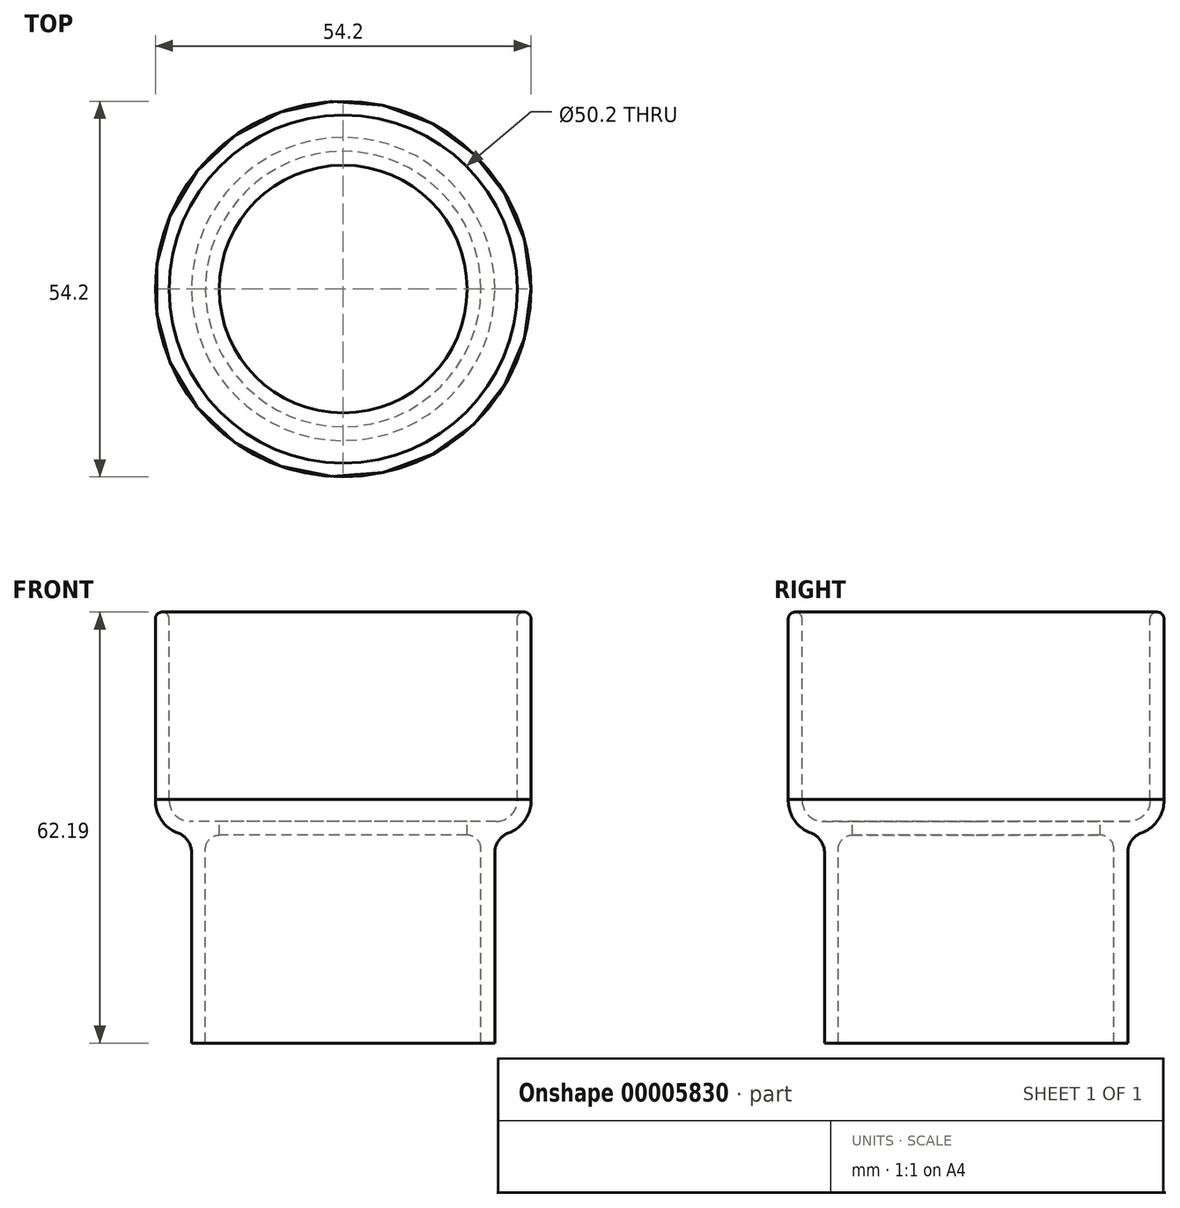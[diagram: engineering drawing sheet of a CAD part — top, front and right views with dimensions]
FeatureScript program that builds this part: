
annotation { "Feature Type Name" : "Feature", "Feature Type Description" : "" }
export const myFeature = defineFeature(function(context is Context, id is Id, definition is map)
    precondition{}
    {
        {
            var Q0;
            Q0=qCreatedBy(makeId("Front.planeOp"),FACE);
            var sketch = newSketch(context, id + "F0", { "sketchPlane" : qUnion([Q0])});
            skLineSegment(sketch, "E0.right", {"start": v(-27.1, 62.19) * mm, "end": v(-27.1, 35.18) * mm});
            skLineSegment(sketch, "E1", {"start": v(-25.1, 62.19) * mm, "end": v(-25.1, 35) * mm});
            skLineSegment(sketch, "E2", {"start": v(-19.88, 0) * mm, "end": v(-19.88, 28) * mm});
            skPoint(sketch, "E3.orphan", {"position": v(-25.1, 0) * mm});
            skLineSegment(sketch, "E4.bottom", {"start": v(-17.88, 30) * mm, "end": v(-17.88, 30) * mm});
            skLineSegment(sketch, "E4.top", {"start": v(-22.1, 32) * mm, "end": v(-17.88, 32) * mm});
            skLineSegment(sketch, "E4.right", {"start": v(-17.88, 30) * mm, "end": v(-17.88, 32) * mm});
            skLineSegment(sketch, "E5", {"start": v(0, 62.19) * mm, "end": v(0, 0) * mm, "construction": true});
            skLineSegment(sketch, "E6", {"start": v(-19.88, 0) * mm, "end": v(0, 0) * mm});
            skLineSegment(sketch, "E7", {"start": v(0, 62.19) * mm, "end": v(27.1, 62.19) * mm});
            skLineSegment(sketch, "E8", {"start": v(-27.1, 62.19) * mm, "end": v(0, 62.19) * mm});
            skLineSegment(sketch, "E9", {"start": v(-21.87, 22.19) * mm, "end": v(0, 22.19) * mm, "construction": true});
            skLineSegment(sketch, "E10", {"start": v(0, 22.19) * mm, "end": v(27.8, 22.19) * mm, "construction": true});
            skLineSegment(sketch, "E11", {"start": v(0, 0) * mm, "end": v(19.88, 0) * mm});
            skLineSegment(sketch, "E12", {"start": v(-21.87, 27.5) * mm, "end": v(-21.88, 0) * mm});
            skLineSegment(sketch, "E13.trimOffspring", {"start": v(-21.88, 0) * mm, "end": v(-19.88, 0) * mm});
            skPoint(sketch, "E14.visualSharp", {"position": v(-25.1, 32) * mm});
            skArc(sketch, "E14.filletArc", {"start": v(-25.1, 35) * mm, "mid": v(-24.22, 32.88) * mm, "end": v(-22.1, 32) * mm});
            skArc(sketch, "E15.0", {"start": v(-27.1, 35.18) * mm, "mid": v(-26.26, 32.21) * mm, "end": v(-23.83, 30.3) * mm});
            skPoint(sketch, "E16.start.orphan", {"position": v(-27.1, 22.19) * mm});
            skPoint(sketch, "E17.visualSharp", {"position": v(-21.87, 30) * mm});
            skArc(sketch, "E17.filletArc", {"start": v(-21.87, 27.5) * mm, "mid": v(-22.41, 29.2) * mm, "end": v(-23.83, 30.3) * mm});
            skPoint(sketch, "E18.visualSharp", {"position": v(-19.88, 30) * mm});
            skArc(sketch, "E18.filletArc", {"start": v(-17.88, 30) * mm, "mid": v(-19.29, 29.41) * mm, "end": v(-19.88, 28) * mm});
            skSolve(sketch);
        }
        {
            var Q0;
            Q0=makeQuery(id+"F0.imprint","IMPRINT",FACE,{"disambiguationData":[TD([[makeQuery(id+"F0.imprint","IMPRINT",EDGE,{"derivedFrom":sQuery(id+"F0.wireOp",EDGE,"E0.bottom")}),1.0]])]});
            var Q1;
            {var subQ1=sQuery(id+"F0.wireOp",EDGE,"E0.right");Q1=makeQuery(id+"F0.imprint","IMPRINT",FACE,{"disambiguationData":[TD([[makeQuery(id+"F0.imprint","IMPRINT",EDGE,{"derivedFrom":subQ1}),1.0]])]});}
            var Q2;
            Q2=sQuery(id+"F0.wireOp",EDGE,"E5");
            revolve(context, id + "F1", {"surfaceOperationType" : NewSurfaceOperationType.NEW, "entities" : qUnion([Q0, Q1]), "axis" : qUnion([Q2]), "revolveType" : RevolveType.FULL});
        }
        {
            var Q0;
            Q0=makeQuery(id+"F1.opRevolve","SWEPT_EDGE",EDGE,{"disambiguationData":[OSD([sQuery(id+"F0.wireOp",EDGE,"E0.right"),sQuery(id+"F0.wireOp",EDGE,"E8")])]});
            var Q1;
            Q1=makeQuery(id+"F1.opRevolve","SWEPT_EDGE",EDGE,{"disambiguationData":[OSD([sQuery(id+"F0.wireOp",EDGE,"E1"),sQuery(id+"F0.wireOp",EDGE,"E8")])]});
            fillet(context, id + "F2", {"entities" : qUnion([Q0, Q1]), "radius" : 1 * mm, "tangentPropagation" : true, "allowEdgeOverflow" : false});
        }
    });
